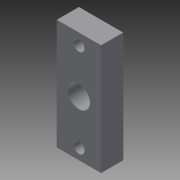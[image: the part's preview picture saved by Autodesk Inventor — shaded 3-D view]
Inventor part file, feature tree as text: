
AUTODESK INVENTOR PART (.ipt)
format: ipt  version: 2014 SP1 (Build 180222100, 222)  size: 90,112 bytes
history: native  units: in
note: dims shown in document units (in); Inventor stores cm internally (conversion verified against a paired STEP export)
features: sketch x3, hole x2, extrude x1
ambient origin geometry x8: Origin, YZ Plane, XZ Plane, XY Plane, X Axis, Y Axis, Z Axis, Center Point
bodies: Solid1 (feature_tree)
feature tree (6):
  extrude  "Extrusion1"  Depth=2.5in
  hole  "Hole2"  [1 undecoded]
  hole  "Hole3"  [1 undecoded]
  sketch  "Sketch1"  dims[d0=1.0in d1=2.5in]
  sketch  "Sketch2"  dims[d2=0.5in d3=0.0in d4=0.25in]
  sketch  "Sketch3"  dims[d5=0.25in d13=0.25in d14=0.75in d15=0.375in d16=0.25in d17=0.5635in d18=1.0in d19=0.8108in d20=0.5in d21=0.75in d22=0.375in d23=0.25in d24=0.5635in d25=1.0in d26=0.8108in]
note: 2 required parameter values undecoded (feature->parameter linkage not recoverable at this tier; creation-order binding heuristic only, values carry confidence <= 0.55)
